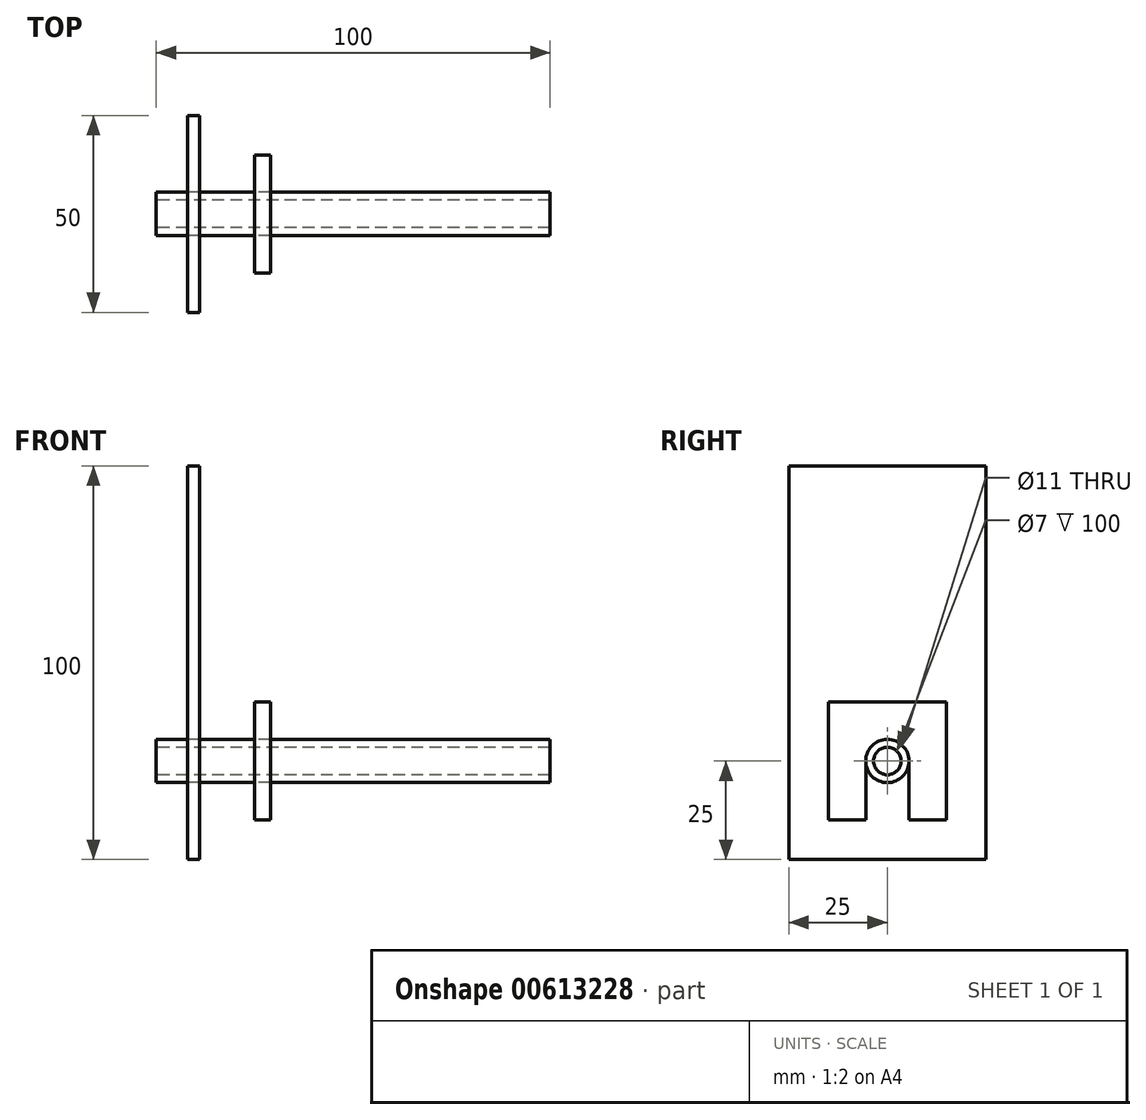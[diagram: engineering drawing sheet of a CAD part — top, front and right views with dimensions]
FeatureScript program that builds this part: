
annotation { "Feature Type Name" : "Feature", "Feature Type Description" : "" }
export const myFeature = defineFeature(function(context is Context, id is Id, definition is map)
    precondition{}
    {
        {
            var Q0;
            Q0=qCreatedBy(makeId("Right.planeOp"),FACE);
            var sketch = newSketch(context, id + "F0", { "sketchPlane" : qUnion([Q0])});
            skCircle(sketch, "E0", {"center": v(0, 0) * mm, "radius": 5.5 * mm});
            skCircle(sketch, "E1", {"center": v(0, 0) * mm, "radius": 3.5 * mm});
            skSolve(sketch);
        }
        {
            var Q0;
            Q0=makeQuery(id+"F0.imprint","IMPRINT",FACE,{"disambiguationData":[TD([[makeQuery(id+"F0.imprint","IMPRINT",EDGE,{"derivedFrom":sQuery(id+"F0.wireOp",EDGE,"E0")}),1.0]])]});
            extrude(context, id + "F1", {"entities" : qUnion([Q0]), "depth" : 100 * mm, "offsetDistance" : 25 * mm});
        }
        {
            var Q0;
            Q0=qCreatedBy(makeId("Right.planeOp"),FACE);
            cPlane(context, id + "F2", {"entities" : qUnion([Q0]), "cplaneType" : CPlaneType.OFFSET, "offset" : 8 * mm, "width" : 150 * mm, "height" : 150 * mm});
        }
        {
            var Q0;
            Q0=qCreatedBy(makeId("Right.planeOp"),FACE);
            cPlane(context, id + "F3", {"entities" : qUnion([Q0]), "cplaneType" : CPlaneType.OFFSET, "offset" : 25 * mm, "width" : 150 * mm, "height" : 150 * mm});
        }
        {
            var Q0;
            Q0=qCreatedBy(id+"F2.planeOp",FACE);
            var sketch = newSketch(context, id + "F4", { "sketchPlane" : qUnion([Q0])});
            skCircle(sketch, "E2", {"center": v(0, 0) * mm, "radius": 5.5 * mm});
            skLineSegment(sketch, "E3.bottom", {"start": v(-25, 75) * mm, "end": v(25, 75) * mm});
            skLineSegment(sketch, "E3.top", {"start": v(-25, -25) * mm, "end": v(25, -25) * mm});
            skLineSegment(sketch, "E3.left", {"start": v(-25, 75) * mm, "end": v(-25, -25) * mm});
            skLineSegment(sketch, "E3.right", {"start": v(25, 75) * mm, "end": v(25, -25) * mm});
            skSolve(sketch);
        }
        {
            var Q0;
            Q0=makeQuery(id+"F4.imprint","IMPRINT",FACE,{"disambiguationData":[TD([[makeQuery(id+"F4.imprint","IMPRINT",EDGE,{"derivedFrom":sQuery(id+"F4.wireOp",EDGE,"E2")}),-1.0]])]});
            extrude(context, id + "F5", {"entities" : qUnion([Q0]), "depth" : 3 * mm, "offsetDistance" : 25 * mm});
        }
        {
            var Q0;
            Q0=qCreatedBy(id+"F3.planeOp",FACE);
            var sketch = newSketch(context, id + "F6", { "sketchPlane" : qUnion([Q0])});
            skCircle(sketch, "E4", {"center": v(0, 0) * mm, "radius": 5.5 * mm});
            skLineSegment(sketch, "E5.bottom", {"start": v(-15, 15) * mm, "end": v(15, 15) * mm});
            skLineSegment(sketch, "E5.top", {"start": v(-15, -15) * mm, "end": v(15, -15) * mm});
            skLineSegment(sketch, "E5.left", {"start": v(-15, 15) * mm, "end": v(-15, -15) * mm});
            skLineSegment(sketch, "E5.right", {"start": v(15, 15) * mm, "end": v(15, -15) * mm});
            skLineSegment(sketch, "E6", {"start": v(-5.5, 0) * mm, "end": v(5.5, 0) * mm});
            skLineSegment(sketch, "E7", {"start": v(-5.5, 0) * mm, "end": v(-5.5, -15) * mm});
            skLineSegment(sketch, "E8", {"start": v(5.5, 0) * mm, "end": v(5.5, -15) * mm});
            skPoint(sketch, "E9.orphan", {"position": v(-15, 0) * mm});
            skPoint(sketch, "E10.orphan", {"position": v(15, 0) * mm});
            skSolve(sketch);
        }
        {
            var Q0;
            Q0=makeQuery(id+"F6.imprint","IMPRINT",FACE,{"disambiguationData":[TD([[makeQuery(id+"F6.imprint","IMPRINT",EDGE,{"derivedFrom":sQuery(id+"F6.wireOp",EDGE,"E5.bottom")}),-1.0]])]});
            extrude(context, id + "F7", {"entities" : qUnion([Q0]), "depth" : 4 * mm, "offsetDistance" : 25 * mm});
        }
    });
